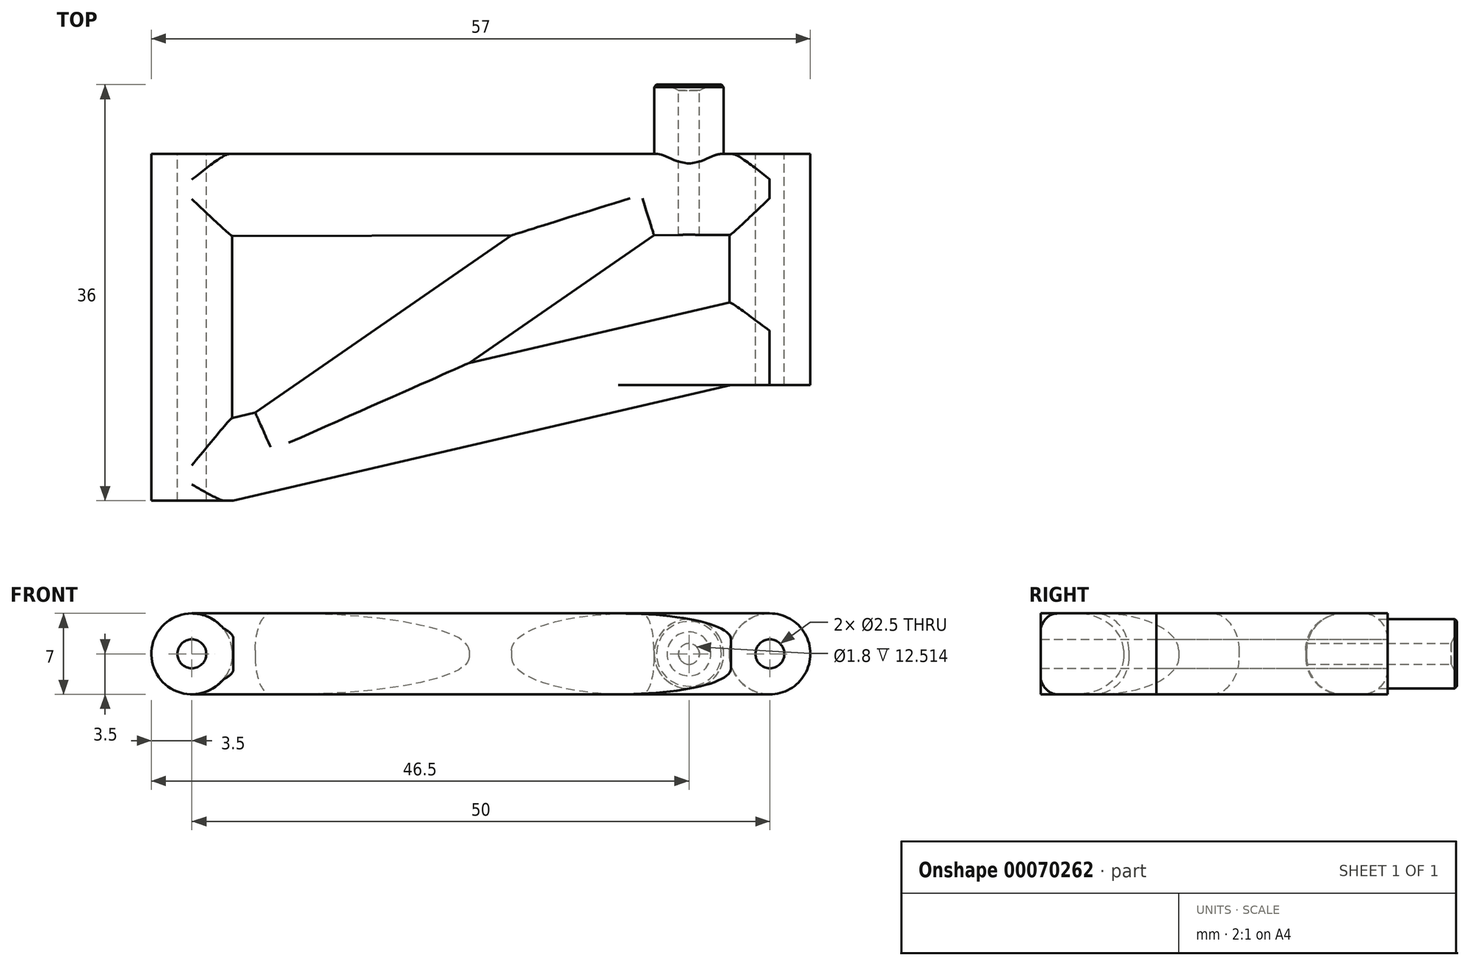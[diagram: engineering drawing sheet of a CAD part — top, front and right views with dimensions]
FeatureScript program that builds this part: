
annotation { "Feature Type Name" : "Feature", "Feature Type Description" : "" }
export const myFeature = defineFeature(function(context is Context, id is Id, definition is map)
    precondition{}
    {
        {
            var Q0;
            Q0=qCreatedBy(makeId("Front.planeOp"),FACE);
            var sketch = newSketch(context, id + "F0", { "sketchPlane" : qUnion([Q0])});
            skCircle(sketch, "E0", {"center": v(0, 0) * mm, "radius": 1.25 * mm});
            skCircle(sketch, "E1", {"center": v(0, 0) * mm, "radius": 3.5 * mm});
            skCircle(sketch, "E2", {"center": v(50, 0) * mm, "radius": 1.25 * mm});
            skCircle(sketch, "E3", {"center": v(50, 0) * mm, "radius": 3.5 * mm});
            skSolve(sketch);
        }
        {
            var Q0;
            Q0=makeQuery(id+"F0.imprint","IMPRINT",FACE,{"disambiguationData":[TD([[makeQuery(id+"F0.imprint","IMPRINT",EDGE,{"derivedFrom":sQuery(id+"F0.wireOp",EDGE,"E0")}),-1.0]])]});
            extrude(context, id + "F1", {"entities" : qUnion([Q0]), "depth" : 30 * mm});
        }
        {
            var Q0;
            Q0=makeQuery(id+"F0.imprint","IMPRINT",FACE,{"disambiguationData":[TD([[makeQuery(id+"F0.imprint","IMPRINT",EDGE,{"derivedFrom":sQuery(id+"F0.wireOp",EDGE,"E2")}),-1.0]])]});
            extrude(context, id + "F2", {"entities" : qUnion([Q0]), "depth" : 20 * mm});
        }
        {
            var Q0;
            Q0=qCreatedBy(makeId("Top.planeOp"),FACE);
            var sketch = newSketch(context, id + "F3", { "sketchPlane" : qUnion([Q0])});
            skLineSegment(sketch, "E4", {"start": v(0, 0) * mm, "end": v(49.97, 0) * mm});
            skLineSegment(sketch, "E5", {"start": v(49.97, 0) * mm, "end": v(49.97, -7) * mm});
            skLineSegment(sketch, "E6", {"start": v(49.97, -20) * mm, "end": v(46.62, -20) * mm});
            skLineSegment(sketch, "E7", {"start": v(46.62, -20) * mm, "end": v(3.6, -30) * mm});
            skLineSegment(sketch, "E8", {"start": v(3.6, -30) * mm, "end": v(0, -30) * mm});
            skLineSegment(sketch, "E9", {"start": v(0, -30) * mm, "end": v(0, -23.65) * mm});
            skLineSegment(sketch, "E10.trimOffspring", {"start": v(49.97, -12.03) * mm, "end": v(49.97, -20) * mm});
            skLineSegment(sketch, "E11.trimOffspring", {"start": v(0, -7.1) * mm, "end": v(0, 0) * mm});
            skPoint(sketch, "E12.orphan", {"position": v(0, -7) * mm});
            skLineSegment(sketch, "E13", {"start": v(0, -7.1) * mm, "end": v(27.64, -7.04) * mm});
            skLineSegment(sketch, "E14", {"start": v(0, -23.65) * mm, "end": v(5.48, -22.37) * mm});
            skLineSegment(sketch, "E15", {"start": v(39.97, -7.02) * mm, "end": v(24, -18.07) * mm});
            skLineSegment(sketch, "E16.trimOffspring", {"start": v(27.64, -7.04) * mm, "end": v(5.48, -22.37) * mm});
            skLineSegment(sketch, "E17.trimOffspring", {"start": v(39.97, -7.02) * mm, "end": v(49.97, -7) * mm});
            skLineSegment(sketch, "E18.trimOffspring", {"start": v(24, -18.07) * mm, "end": v(49.97, -12.03) * mm});
            skSolve(sketch);
        }
        {
            var Q0;
            Q0=makeQuery(id+"F3.imprint","IMPRINT",FACE,{"disambiguationData":[TD([[makeQuery(id+"F3.imprint","IMPRINT",EDGE,{"derivedFrom":sQuery(id+"F3.wireOp",EDGE,"E4")}),-1.0]])]});
            extrude(context, id + "F4", {"entities" : qUnion([Q0]), "operationType" : NewBodyOperationType.ADD, "endBound" : BoundingType.SYMMETRIC, "depth" : 7 * mm});
        }
        {
            var Q0;
            {var subQ0=sQuery(id+"F3.wireOp",EDGE,"E4");var subQ1=sQuery(id+"F3.wireOp",EDGE,"E5");Q0=makeQuery(id+"F4.boolean.opBoolean","SPLIT",EDGE,{"disambiguationData":[TD([makeQuery(id+"F4.opExtrude","SWEPT_FACE",FACE,{"disambiguationData":[OSD([subQ1])]})])],"derivedFrom":makeQuery(id+"F4.opExtrude","CAP_EDGE",EDGE,{"disambiguationData":[OSD([subQ0])],"isStart":false})});}
            var Q1;
            Q1=makeQuery(id+"F4.opExtrude","CAP_EDGE",EDGE,{"disambiguationData":[OSD([sQuery(id+"F3.wireOp",EDGE,"15c3c0d3-5ffc-412a-9384-ac1cea64b5b4.0")])],"isStart":false});
            var Q2;
            Q2=makeQuery(id+"F4.opExtrude","CAP_EDGE",EDGE,{"disambiguationData":[OSD([sQuery(id+"F3.wireOp",EDGE,"m9PX38mi-AktG-0A8L-kthQ-M864UZ6yBpa6")])],"isStart":false});
            var Q3;
            Q3=makeQuery(id+"F4.opExtrude","CAP_EDGE",EDGE,{"disambiguationData":[OSD([sQuery(id+"F3.wireOp",EDGE,"c7e88b3e-22a9-4dfa-9b9b-7fa8d71041d9.trimOffspring")])],"isStart":false});
            var Q4;
            Q4=makeQuery(id+"F4.opExtrude","CAP_EDGE",EDGE,{"disambiguationData":[OSD([sQuery(id+"F3.wireOp",EDGE,"E7")])],"isStart":false});
            var Q5;
            Q5=makeQuery(id+"F4.opExtrude","CAP_EDGE",EDGE,{"disambiguationData":[OSD([sQuery(id+"F3.wireOp",EDGE,"E7")])],"isStart":true});
            var Q6;
            Q6=makeQuery(id+"F4.opExtrude","CAP_EDGE",EDGE,{"disambiguationData":[OSD([sQuery(id+"F3.wireOp",EDGE,"6OxObJGX-1zM3-HorB-H32U-3rqcHQQTOBs3")])],"isStart":true});
            var Q7;
            Q7=makeQuery(id+"F4.opExtrude","CAP_EDGE",EDGE,{"disambiguationData":[OSD([sQuery(id+"F3.wireOp",EDGE,"9oZ26lmC-GrsE-5xUm-wb6w-0CIcEomgdE0o")])],"isStart":true});
            var Q8;
            Q8=makeQuery(id+"F4.opExtrude","CAP_EDGE",EDGE,{"disambiguationData":[OSD([sQuery(id+"F3.wireOp",EDGE,"c7e88b3e-22a9-4dfa-9b9b-7fa8d71041d9.trimOffspring")])],"isStart":true});
            fillet(context, id + "F5", {"entities" : qUnion([Q0, Q1, Q2, Q3, Q4, Q5, Q6, Q7, Q8]), "radius" : 2.2 * mm, "tangentPropagation" : true, "allowEdgeOverflow" : false});
        }
        {
            var Q0;
            Q0=makeQuery(id+"F0.imprint","IMPRINT",FACE,{"disambiguationData":[TD([[makeQuery(id+"F0.imprint","IMPRINT",EDGE,{"derivedFrom":sQuery(id+"F0.wireOp",EDGE,"E2")}),1.0]])]});
            var Q1;
            Q1=makeQuery(id+"F0.imprint","IMPRINT",FACE,{"disambiguationData":[TD([[makeQuery(id+"F0.imprint","IMPRINT",EDGE,{"derivedFrom":sQuery(id+"F0.wireOp",EDGE,"E0")}),1.0]])]});
            extrude(context, id + "F6", {"entities" : qUnion([Q0, Q1]), "operationType" : NewBodyOperationType.REMOVE, "endBound" : BoundingType.THROUGH_ALL, "depth" : 25 * mm});
        }
        {
            var Q0;
            Q0=qCreatedBy(makeId("Front.planeOp"),FACE);
            var sketch = newSketch(context, id + "F7", { "sketchPlane" : qUnion([Q0])});
            skCircle(sketch, "E19", {"center": v(43, 0) * mm, "radius": 3 * mm});
            skCircle(sketch, "E20", {"center": v(43, 0) * mm, "radius": 0.9 * mm});
            skSolve(sketch);
        }
        {
            var Q0;
            Q0=qSketchRegion(id+"F7",true);
            extrude(context, id + "F8", {"entities" : qUnion([Q0]), "operationType" : NewBodyOperationType.ADD, "depth" : 7 * mm, "hasSecondDirection" : true, "secondDirectionOppositeDirection" : true, "secondDirectionDepth" : 6 * mm});
        }
        {
            var Q0;
            Q0=makeQuery(id+"F8.boolean.opBoolean","SPLIT",FACE,{"disambiguationData":[TD([makeQuery(id+"F8.opExtrude","SWEPT_FACE",FACE,{"disambiguationData":[OSD([sQuery(id+"F7.wireOp",EDGE,"E20")])]})])],"derivedFrom":makeQuery(id+"F4.boolean.opBoolean","MERGE",FACE,{"derivedFrom":[makeQuery(id+"F1.opExtrude","CAP_FACE",FACE,{"disambiguationData":[OSD([sQuery(id+"F0.wireOp",EDGE,"E0"),sQuery(id+"F0.wireOp",EDGE,"E1")])],"isStart":true}),makeQuery(id+"F2.opExtrude","CAP_FACE",FACE,{"disambiguationData":[OSD([sQuery(id+"F0.wireOp",EDGE,"E2"),sQuery(id+"F0.wireOp",EDGE,"E3")])],"isStart":true}),makeQuery(id+"F4.opExtrude","SWEPT_FACE",FACE,{"disambiguationData":[OSD([sQuery(id+"F3.wireOp",EDGE,"E4")])]})]})});
            extrude(context, id + "F9", {"entities" : qUnion([Q0]), "operationType" : NewBodyOperationType.REMOVE, "oppositeDirection" : true, "depth" : 10.62 * mm});
        }
        {
            var Q0;
            Q0=makeQuery(id+"F0.imprint","IMPRINT",FACE,{"disambiguationData":[TD([[makeQuery(id+"F0.imprint","IMPRINT",EDGE,{"derivedFrom":sQuery(id+"F0.wireOp",EDGE,"E0")}),-1.0]])]});
            extrude(context, id + "F10", {"entities" : qUnion([Q0]), "operationType" : NewBodyOperationType.ADD, "depth" : 30 * mm});
        }
        {
            var Q0;
            Q0=makeQuery(id+"F0.imprint","IMPRINT",FACE,{"disambiguationData":[TD([[makeQuery(id+"F0.imprint","IMPRINT",EDGE,{"derivedFrom":sQuery(id+"F0.wireOp",EDGE,"E2")}),-1.0]])]});
            extrude(context, id + "F11", {"entities" : qUnion([Q0]), "operationType" : NewBodyOperationType.ADD, "depth" : 20 * mm});
        }
        {
            var Q0;
            Q0=makeQuery(id+"F8.opExtrude","CAP_EDGE",EDGE,{"disambiguationData":[OSD([sQuery(id+"F7.wireOp",EDGE,"E20")])],"isStart":true});
            chamfer(context, id + "F12", {"entities" : qUnion([Q0]), "chamferType" : ChamferType.TWO_OFFSETS, "width1" : 1 * mm, "oppositeDirection" : false, "width2" : .5 * mm, "tangentPropagation" : true});
        }
        {
            var Q0;
            Q0=makeQuery(id+"F4.opExtrude","CAP_EDGE",EDGE,{"disambiguationData":[OSD([sQuery(id+"F3.wireOp",EDGE,"E13")])],"isStart":false});
            var Q1;
            Q1=makeQuery(id+"F4.opExtrude","CAP_EDGE",EDGE,{"disambiguationData":[OSD([sQuery(id+"F3.wireOp",EDGE,"E16.trimOffspring")])],"isStart":false});
            var Q2;
            Q2=makeQuery(id+"F4.opExtrude","CAP_EDGE",EDGE,{"disambiguationData":[OSD([sQuery(id+"F3.wireOp",EDGE,"E15")])],"isStart":false});
            var Q3;
            Q3=makeQuery(id+"F4.opExtrude","CAP_EDGE",EDGE,{"disambiguationData":[OSD([sQuery(id+"F3.wireOp",EDGE,"E17.trimOffspring")])],"isStart":false});
            var Q4;
            Q4=makeQuery(id+"F4.opExtrude","CAP_EDGE",EDGE,{"disambiguationData":[OSD([sQuery(id+"F3.wireOp",EDGE,"E18.trimOffspring")])],"isStart":false});
            var Q5;
            Q5=makeQuery(id+"F4.opExtrude","CAP_EDGE",EDGE,{"disambiguationData":[OSD([sQuery(id+"F3.wireOp",EDGE,"E14")])],"isStart":false});
            var Q6;
            Q6=makeQuery(id+"F4.opExtrude","CAP_EDGE",EDGE,{"disambiguationData":[OSD([sQuery(id+"F3.wireOp",EDGE,"E13")])],"isStart":true});
            var Q7;
            Q7=makeQuery(id+"F4.opExtrude","CAP_EDGE",EDGE,{"disambiguationData":[OSD([sQuery(id+"F3.wireOp",EDGE,"E16.trimOffspring")])],"isStart":true});
            var Q8;
            Q8=makeQuery(id+"F4.opExtrude","CAP_EDGE",EDGE,{"disambiguationData":[OSD([sQuery(id+"F3.wireOp",EDGE,"E15")])],"isStart":true});
            var Q9;
            Q9=makeQuery(id+"F4.opExtrude","CAP_EDGE",EDGE,{"disambiguationData":[OSD([sQuery(id+"F3.wireOp",EDGE,"E18.trimOffspring")])],"isStart":true});
            var Q10;
            Q10=makeQuery(id+"F4.opExtrude","CAP_EDGE",EDGE,{"disambiguationData":[OSD([sQuery(id+"F3.wireOp",EDGE,"E17.trimOffspring")])],"isStart":true});
            var Q11;
            Q11=makeQuery(id+"F4.opExtrude","CAP_EDGE",EDGE,{"disambiguationData":[OSD([sQuery(id+"F3.wireOp",EDGE,"E14")])],"isStart":true});
            fillet(context, id + "F13", {"entities" : qUnion([Q0, Q1, Q2, Q3, Q4, Q5, Q6, Q7, Q8, Q9, Q10, Q11]), "radius" : 3.2 * mm, "tangentPropagation" : true, "allowEdgeOverflow" : false});
        }
        {
            var Q0;
            Q0=makeQuery(id+"F8.opExtrude","CAP_EDGE",EDGE,{"disambiguationData":[OSD([sQuery(id+"F7.wireOp",EDGE,"E19")])],"isStart":true});
            chamfer(context, id + "F14", {"entities" : qUnion([Q0]), "width" : .2 * mm, "tangentPropagation" : true});
        }
    });
